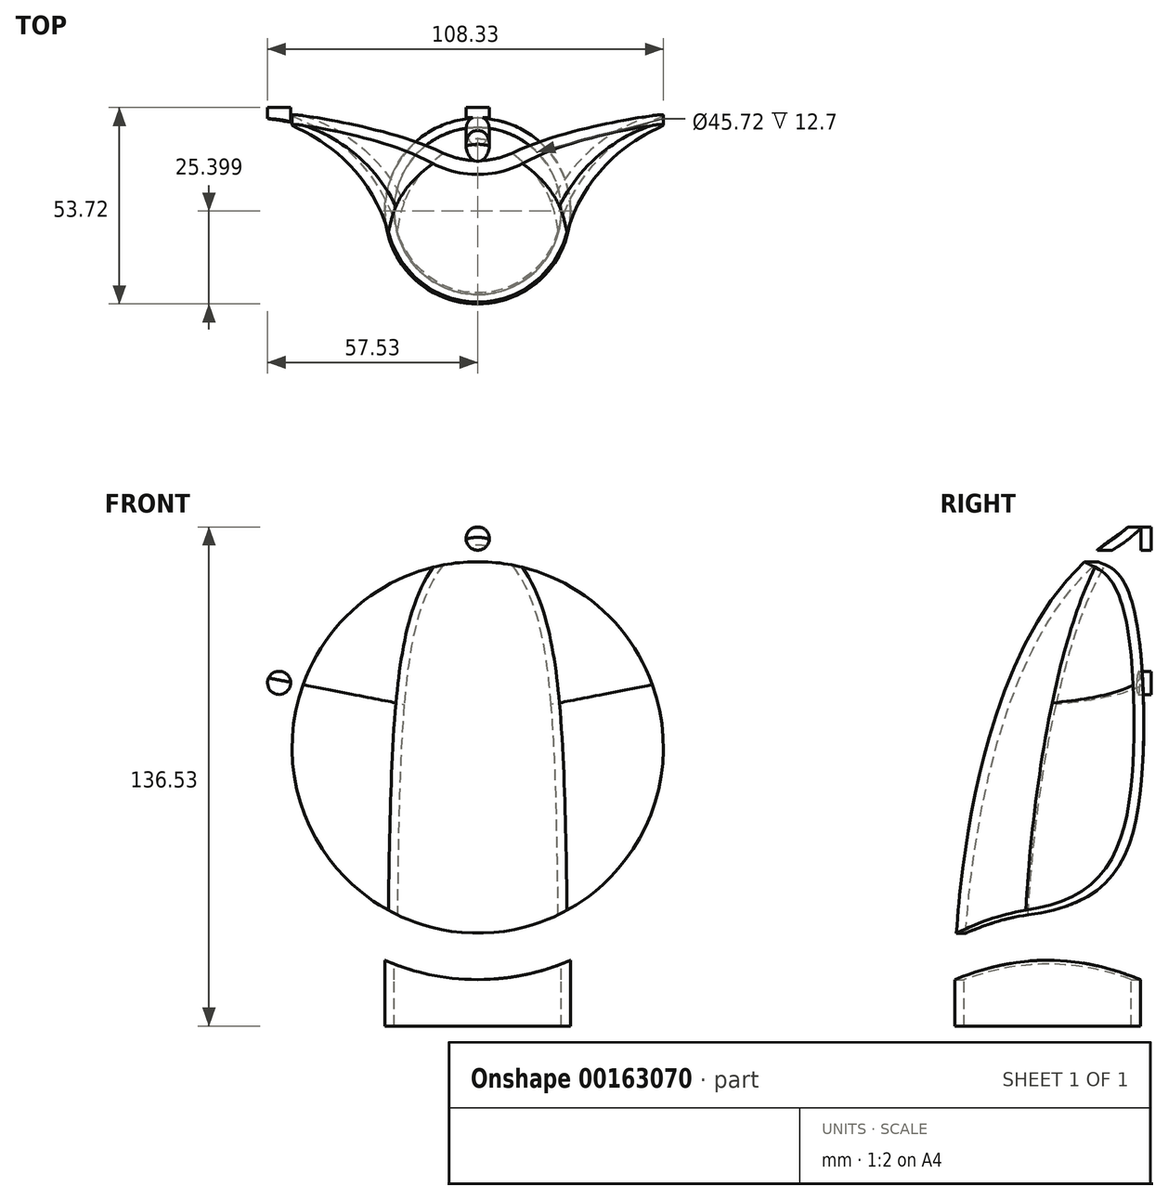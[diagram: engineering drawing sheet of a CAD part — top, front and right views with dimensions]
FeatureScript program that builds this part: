
annotation { "Feature Type Name" : "Feature", "Feature Type Description" : "" }
export const myFeature = defineFeature(function(context is Context, id is Id, definition is map)
    precondition{}
    {
        {
            var Q0;
            Q0=qCreatedBy(makeId("Top.planeOp"),FACE);
            cPlane(context, id + "F0", {"entities" : qUnion([Q0]), "cplaneType" : CPlaneType.OFFSET, "offset" : 63.5 * mm, "oppositeDirection" : true, "width" : 152.4 * mm, "height" : 152.4 * mm});
        }
        {
            var Q0;
            Q0=qCreatedBy(makeId("Front.planeOp"),FACE);
            var sketch = newSketch(context, id + "F1", { "sketchPlane" : qUnion([Q0])});
            skCircle(sketch, "E0", {"center": v(0, 0) * mm, "radius": 63.5 * mm});
            skSolve(sketch);
        }
        {
            var Q0;
            Q0 = qSketchRegion(id + "F1", true);
            extrude(context, id + "F2", {"entities" : qUnion([Q0]), "depth" : 2.92 * mm, "offsetDistance" : 25.4 * mm});
        }
        {
            var Q0;
            Q0=qCreatedBy(id+"F0.planeOp",FACE);
            var sketch = newSketch(context, id + "F3", { "sketchPlane" : qUnion([Q0])});
            skCircle(sketch, "E1", {"center": v(0, -28.32) * mm, "radius": 25.4 * mm});
            skLineSegment(sketch, "E2", {"start": v(-25.4, -28.32) * mm, "end": v(25.4, -28.32) * mm});
            skSolve(sketch);
        }
        {
            var Q0;
            Q0=qCreatedBy(makeId("Right.planeOp"),FACE);
            var sketch = newSketch(context, id + "F4", { "sketchPlane" : qUnion([Q0])});
            skFitSpline(sketch, "E3", {"points": [v(20.38, 41.43) * mm, v(-28.32, -63.5) * mm], "startDerivative": vector(-124.43, 0) * mm, "endDerivative": vector(0, -63.87) * mm});
            skSolve(sketch);
        }
        {
            var Q0;
            {var subQ0=sQuery(id+"F3.wireOp",EDGE,"E2");Q0=makeQuery(id+"F3.imprint","IMPRINT",FACE,{"disambiguationData":[TD([[makeQuery(id+"F3.imprint","IMPRINT",EDGE,{"derivedFrom":subQ0}),1.0]])]});}
            var Q1;
            {var subQ0=sQuery(id+"F3.wireOp",EDGE,"E2");Q1=makeQuery(id+"F3.imprint","IMPRINT",FACE,{"disambiguationData":[TD([[makeQuery(id+"F3.imprint","IMPRINT",EDGE,{"derivedFrom":subQ0}),-1.0]])]});}
            var Q2;
            Q2=sQuery(id+"F4.wireOp",EDGE,"E3");
            sweep(context, id + "F5", {"operationType" : NewBodyOperationType.ADD, "profiles" : qUnion([Q0, Q1]), "path" : qUnion([Q2])});
        }
        {
            var Q0;
            Q0=qCreatedBy(makeId("Right.planeOp"),FACE);
            var sketch = newSketch(context, id + "F6", { "sketchPlane" : qUnion([Q0])});
            skLineSegment(sketch, "E4.bottom", {"start": v(0, 69.49) * mm, "end": v(23.98, 69.49) * mm});
            skLineSegment(sketch, "E4.top", {"start": v(0, -61.52) * mm, "end": v(23.98, -61.52) * mm});
            skLineSegment(sketch, "E4.left", {"start": v(0, 69.49) * mm, "end": v(0, -61.52) * mm});
            skLineSegment(sketch, "E4.right", {"start": v(23.98, 69.49) * mm, "end": v(23.98, -61.52) * mm});
            skSolve(sketch);
        }
        {
            var Q0;
            Q0 = qSketchRegion(id + "F6", true);
            extrude(context, id + "F7", {"entities" : qUnion([Q0]), "operationType" : NewBodyOperationType.REMOVE, "endBound" : BoundingType.THROUGH_ALL, "oppositeDirection" : true, "depth" : 25.4 * mm, "offsetDistance" : 25.4 * mm, "hasSecondDirection" : true, "secondDirectionBound" : SecondDirectionBoundingType.THROUGH_ALL, "secondDirectionOppositeDirection" : false, "secondDirectionDepth" : 25.4 * mm});
        }
        {
            var Q0;
            Q0=makeQuery(id+"F5.boolean.opBoolean","INTERSECT",EDGE,{"derivedFrom":[makeQuery(id+"F2.opExtrude","CAP_FACE",FACE,{"disambiguationData":[OSD([sQuery(id+"F1.wireOp",EDGE,"E0")])],"isStart":false}),makeQuery(id+"F5.opSweep","SWEPT_FACE",FACE,{"disambiguationData":[OSD([sQuery(id+"F3.wireOp",EDGE,"E1"),sQuery(id+"F4.wireOp",EDGE,"E3")])]})]});
            fillet(context, id + "F8", {"entities" : qUnion([Q0]), "radius" : 43.18 * mm, "tangentPropagation" : true, "allowEdgeOverflow" : false});
        }
        {
            var Q0;
            {var subQ0=sQuery(id+"F3.wireOp",EDGE,"E2");Q0=makeQuery(id+"F3.imprint","IMPRINT",FACE,{"disambiguationData":[TD([[makeQuery(id+"F3.imprint","IMPRINT",EDGE,{"derivedFrom":subQ0}),-1.0]])]});}
            var Q1;
            {var subQ0=sQuery(id+"F3.wireOp",EDGE,"E2");Q1=makeQuery(id+"F3.imprint","IMPRINT",FACE,{"disambiguationData":[TD([[makeQuery(id+"F3.imprint","IMPRINT",EDGE,{"derivedFrom":subQ0}),1.0]])]});}
            extrude(context, id + "F9", {"entities" : qUnion([Q0, Q1]), "operationType" : NewBodyOperationType.ADD, "oppositeDirection" : true, "depth" : 12.7 * mm, "offsetDistance" : 25.4 * mm});
        }
        {
            var Q0;
            Q0=makeQuery(id+"F7.boolean.opBoolean","MERGE",FACE,{"derivedFrom":[makeQuery(id+"F2.opExtrude","CAP_FACE",FACE,{"disambiguationData":[OSD([sQuery(id+"F1.wireOp",EDGE,"E0")])],"isStart":true}),makeQuery(id+"F7.opExtrude","SWEPT_FACE",FACE,{"disambiguationData":[OSD([sQuery(id+"F6.wireOp",EDGE,"E4.left")])]})]});
            var Q1;
            Q1=makeQuery(id+"F9.opExtrude","CAP_FACE",FACE,{"disambiguationData":[OSD([sQuery(id+"F3.wireOp",EDGE,"E1")])],"isStart":false});
            shell(context, id + "F10", {"entities" : qUnion([Q0, Q1]), "thickness" : 2.54 * mm});
        }
        {
            var Q0;
            Q0=qCreatedBy(makeId("Front.planeOp"),FACE);
            var sketch = newSketch(context, id + "F11", { "sketchPlane" : qUnion([Q0])});
            skCircle(sketch, "E5", {"center": v(0, 0) * mm, "radius": 63.5 * mm});
            skCircle(sketch, "E6", {"center": v(0, 0) * mm, "radius": 50.8 * mm});
            skSolve(sketch);
        }
        {
            var Q0;
            Q0 = qSketchRegion(id + "F11", true);
            extrude(context, id + "F12", {"entities" : qUnion([Q0]), "operationType" : NewBodyOperationType.ADD, "depth" : 2.8 * mm, "offsetDistance" : 25.4 * mm});
        }
        {
            var Q0;
            Q0=makeQuery(id+"F2.opExtrude","SWEPT_BODY",BODY,{"disambiguationData":[OSD([sQuery(id+"F1.wireOp",EDGE,"E0")])]});
            transform(context, id + "F13", {"entities" : qUnion([Q0]), "transformType" : TransformType.TRANSLATION_3D, "dx" : 0 * mm, "dy" : 0 * mm, "dz" : 0 * mm, "makeCopy" : true});
        }
        {
            var Q0;
            Q0=makeQuery(id+"F12.boolean.opBoolean","MERGE",FACE,{"derivedFrom":[makeQuery(id+"F7.boolean.opBoolean","MERGE",FACE,{"derivedFrom":[makeQuery(id+"F2.opExtrude","CAP_FACE",FACE,{"disambiguationData":[OSD([sQuery(id+"F1.wireOp",EDGE,"E0")])],"isStart":true}),makeQuery(id+"F7.opExtrude","SWEPT_FACE",FACE,{"disambiguationData":[OSD([sQuery(id+"F6.wireOp",EDGE,"E4.left")])]})]}),makeQuery(id+"F12.opExtrude","CAP_FACE",FACE,{"disambiguationData":[OSD([sQuery(id+"F11.wireOp",EDGE,"E5"),sQuery(id+"F11.wireOp",EDGE,"E6")])],"isStart":true})]});
            var sketch = newSketch(context, id + "F14", { "sketchPlane" : qUnion([Q0])});
            skCircle(sketch, "E7", {"center": v(0, 0) * mm, "radius": 57.15 * mm});
            skCircle(sketch, "E8", {"center": v(0, 57.15) * mm, "radius": 3.18 * mm});
            skCircle(sketch, "E9.1.0", {"center": v(-54.35, 17.66) * mm, "radius": 3.18 * mm});
            skCircle(sketch, "E9.2.0", {"center": v(-33.6, -46.24) * mm, "radius": 3.18 * mm});
            skCircle(sketch, "E9.3.0", {"center": v(33.6, -46.24) * mm, "radius": 3.18 * mm});
            skCircle(sketch, "E9.4.0", {"center": v(54.35, 17.66) * mm, "radius": 3.18 * mm});
            skSolve(sketch);
        }
        {
            var Q0;
            {var subQ0=sQuery(id+"F14.wireOp",EDGE,"E9.2.0");var subQ1=sQuery(id+"F14.wireOp",EDGE,"E7");var subQ2=makeQuery(id+"F14.imprint","INTERSECT",VERTEX,{"disambiguationData":[OD(0.0)],"derivedFrom":[subQ1,subQ0]});Q0=makeQuery(id+"F14.imprint","IMPRINT",FACE,{"disambiguationData":[TD([[makeQuery(id+"F14.imprint","IMPRINT",EDGE,{"disambiguationData":[TD([[subQ2,-1.0]])],"derivedFrom":subQ1}),1.0]])]});}
            var Q1;
            {var subQ0=sQuery(id+"F14.wireOp",EDGE,"E9.2.0");var subQ1=sQuery(id+"F14.wireOp",EDGE,"E7");var subQ2=makeQuery(id+"F14.imprint","INTERSECT",VERTEX,{"disambiguationData":[OD(0.0)],"derivedFrom":[subQ1,subQ0]});Q1=makeQuery(id+"F14.imprint","IMPRINT",FACE,{"disambiguationData":[TD([[makeQuery(id+"F14.imprint","IMPRINT",EDGE,{"disambiguationData":[TD([[subQ2,-1.0]])],"derivedFrom":subQ1}),-1.0]])]});}
            var Q2;
            {var subQ0=sQuery(id+"F14.wireOp",EDGE,"E9.1.0");var subQ1=sQuery(id+"F14.wireOp",EDGE,"E7");var subQ2=makeQuery(id+"F14.imprint","INTERSECT",VERTEX,{"disambiguationData":[OD(0.0)],"derivedFrom":[subQ1,subQ0]});Q2=makeQuery(id+"F14.imprint","IMPRINT",FACE,{"disambiguationData":[TD([[makeQuery(id+"F14.imprint","IMPRINT",EDGE,{"disambiguationData":[TD([[subQ2,-1.0]])],"derivedFrom":subQ1}),1.0]])]});}
            var Q3;
            {var subQ0=sQuery(id+"F14.wireOp",EDGE,"E9.1.0");var subQ1=sQuery(id+"F14.wireOp",EDGE,"E7");var subQ2=makeQuery(id+"F14.imprint","INTERSECT",VERTEX,{"disambiguationData":[OD(0.0)],"derivedFrom":[subQ1,subQ0]});Q3=makeQuery(id+"F14.imprint","IMPRINT",FACE,{"disambiguationData":[TD([[makeQuery(id+"F14.imprint","IMPRINT",EDGE,{"disambiguationData":[TD([[subQ2,-1.0]])],"derivedFrom":subQ1}),-1.0]])]});}
            var Q4;
            {var subQ0=sQuery(id+"F14.wireOp",EDGE,"E8");var subQ1=sQuery(id+"F14.wireOp",EDGE,"E7");var subQ2=makeQuery(id+"F14.imprint","INTERSECT",VERTEX,{"disambiguationData":[OD(0.0)],"derivedFrom":[subQ1,subQ0]});Q4=makeQuery(id+"F14.imprint","IMPRINT",FACE,{"disambiguationData":[TD([[makeQuery(id+"F14.imprint","IMPRINT",EDGE,{"disambiguationData":[TD([[subQ2,-1.0]])],"derivedFrom":subQ1}),1.0]])]});}
            var Q5;
            {var subQ0=sQuery(id+"F14.wireOp",EDGE,"E8");var subQ1=sQuery(id+"F14.wireOp",EDGE,"E7");var subQ2=makeQuery(id+"F14.imprint","INTERSECT",VERTEX,{"disambiguationData":[OD(0.0)],"derivedFrom":[subQ1,subQ0]});Q5=makeQuery(id+"F14.imprint","IMPRINT",FACE,{"disambiguationData":[TD([[makeQuery(id+"F14.imprint","IMPRINT",EDGE,{"disambiguationData":[TD([[subQ2,-1.0]])],"derivedFrom":subQ1}),-1.0]])]});}
            var Q6;
            {var subQ0=sQuery(id+"F14.wireOp",EDGE,"E9.4.0");var subQ1=sQuery(id+"F14.wireOp",EDGE,"E7");var subQ2=makeQuery(id+"F14.imprint","INTERSECT",VERTEX,{"disambiguationData":[OD(0.0)],"derivedFrom":[subQ1,subQ0]});Q6=makeQuery(id+"F14.imprint","IMPRINT",FACE,{"disambiguationData":[TD([[makeQuery(id+"F14.imprint","IMPRINT",EDGE,{"disambiguationData":[TD([[subQ2,1.0]])],"derivedFrom":subQ1}),-1.0]])]});}
            var Q7;
            {var subQ0=sQuery(id+"F14.wireOp",EDGE,"E9.4.0");var subQ1=sQuery(id+"F14.wireOp",EDGE,"E7");var subQ2=makeQuery(id+"F14.imprint","INTERSECT",VERTEX,{"disambiguationData":[OD(0.0)],"derivedFrom":[subQ1,subQ0]});Q7=makeQuery(id+"F14.imprint","IMPRINT",FACE,{"disambiguationData":[TD([[makeQuery(id+"F14.imprint","IMPRINT",EDGE,{"disambiguationData":[TD([[subQ2,1.0]])],"derivedFrom":subQ1}),1.0]])]});}
            var Q8;
            {var subQ0=sQuery(id+"F14.wireOp",EDGE,"E9.3.0");var subQ1=sQuery(id+"F14.wireOp",EDGE,"E7");var subQ2=makeQuery(id+"F14.imprint","INTERSECT",VERTEX,{"disambiguationData":[OD(0.0)],"derivedFrom":[subQ1,subQ0]});Q8=makeQuery(id+"F14.imprint","IMPRINT",FACE,{"disambiguationData":[TD([[makeQuery(id+"F14.imprint","IMPRINT",EDGE,{"disambiguationData":[TD([[subQ2,-1.0]])],"derivedFrom":subQ1}),1.0]])]});}
            var Q9;
            {var subQ0=sQuery(id+"F14.wireOp",EDGE,"E9.3.0");var subQ1=sQuery(id+"F14.wireOp",EDGE,"E7");var subQ2=makeQuery(id+"F14.imprint","INTERSECT",VERTEX,{"disambiguationData":[OD(0.0)],"derivedFrom":[subQ1,subQ0]});Q9=makeQuery(id+"F14.imprint","IMPRINT",FACE,{"disambiguationData":[TD([[makeQuery(id+"F14.imprint","IMPRINT",EDGE,{"disambiguationData":[TD([[subQ2,-1.0]])],"derivedFrom":subQ1}),-1.0]])]});}
            var Q10;
            Q10=sQuery(id+"F14.wireOp",EDGE,"E9.1.0");
            var Q11;
            Q11=sQuery(id+"F14.wireOp",EDGE,"E8");
            var Q12;
            Q12=sQuery(id+"F14.wireOp",EDGE,"E9.4.0");
            var Q13;
            Q13=sQuery(id+"F14.wireOp",EDGE,"E9.3.0");
            var Q14;
            Q14=sQuery(id+"F14.wireOp",EDGE,"E9.2.0");
            extrude(context, id + "F15", {"entities" : qUnion([Q0, Q1, Q2, Q3, Q4, Q5, Q6, Q7, Q8, Q9]), "operationType" : NewBodyOperationType.REMOVE, "surfaceEntities" : qUnion([Q10, Q11, Q12, Q13, Q14]), "endBound" : BoundingType.THROUGH_ALL, "oppositeDirection" : true, "depth" : 25.4 * mm, "offsetDistance" : 25.4 * mm});
        }
        {
            var Q0;
            Q0=makeQuery(id+"F2.opExtrude","SWEPT_BODY",BODY,{"disambiguationData":[OSD([sQuery(id+"F1.wireOp",EDGE,"E0")])]});
            transform(context, id + "F16", {"entities" : qUnion([Q0]), "transformType" : TransformType.TRANSLATION_3D, "dx" : 0 * mm, "dy" : 0 * mm, "dz" : 0 * mm, "makeCopy" : true});
        }
        {
            var Q0;
            Q0=makeQuery(id+"F2.opExtrude","SWEPT_BODY",BODY,{"disambiguationData":[OSD([sQuery(id+"F1.wireOp",EDGE,"E0")])]});
            transform(context, id + "F17", {"entities" : qUnion([Q0]), "transformType" : TransformType.TRANSLATION_3D, "dx" : 0 * mm, "dy" : 0 * mm, "dz" : 0 * mm, "makeCopy" : true});
        }
        {
            var Q0;
            Q0=makeQuery(id+"F17.opPattern","COPY",BODY,{"derivedFrom":makeQuery(id+"F2.opExtrude","SWEPT_BODY",BODY,{"disambiguationData":[OSD([sQuery(id+"F1.wireOp",EDGE,"E0")])]}),"instanceName":"1"});
            deleteBodies(context, id + "F18", {"entities" : qUnion([Q0])});
        }
        {
            var Q0;
            Q0=makeQuery(id+"F16.opPattern","COPY",BODY,{"derivedFrom":makeQuery(id+"F2.opExtrude","SWEPT_BODY",BODY,{"disambiguationData":[OSD([sQuery(id+"F1.wireOp",EDGE,"E0")])]}),"instanceName":"1"});
            deleteBodies(context, id + "F19", {"entities" : qUnion([Q0])});
        }
        {
            var Q0;
            Q0=makeQuery(id+"F13.opPattern","COPY",BODY,{"derivedFrom":makeQuery(id+"F2.opExtrude","SWEPT_BODY",BODY,{"disambiguationData":[OSD([sQuery(id+"F1.wireOp",EDGE,"E0")])]}),"instanceName":"1"});
            deleteBodies(context, id + "F20", {"entities" : qUnion([Q0])});
        }
        {
            var Q0;
            Q0=makeQuery(id+"F2.opExtrude","SWEPT_BODY",BODY,{"disambiguationData":[OSD([sQuery(id+"F1.wireOp",EDGE,"E0")])]});
            transform(context, id + "F21", {"entities" : qUnion([Q0]), "transformType" : TransformType.TRANSLATION_3D, "dx" : 0 * mm, "dy" : 0 * mm, "dz" : 0 * mm, "makeCopy" : true});
        }
        {
            var Q0;
            Q0=makeQuery(id+"F21.opPattern","COPY",BODY,{"derivedFrom":makeQuery(id+"F2.opExtrude","SWEPT_BODY",BODY,{"disambiguationData":[OSD([sQuery(id+"F1.wireOp",EDGE,"E0")])]}),"instanceName":"1"});
            deleteBodies(context, id + "F22", {"entities" : qUnion([Q0])});
        }
    });
